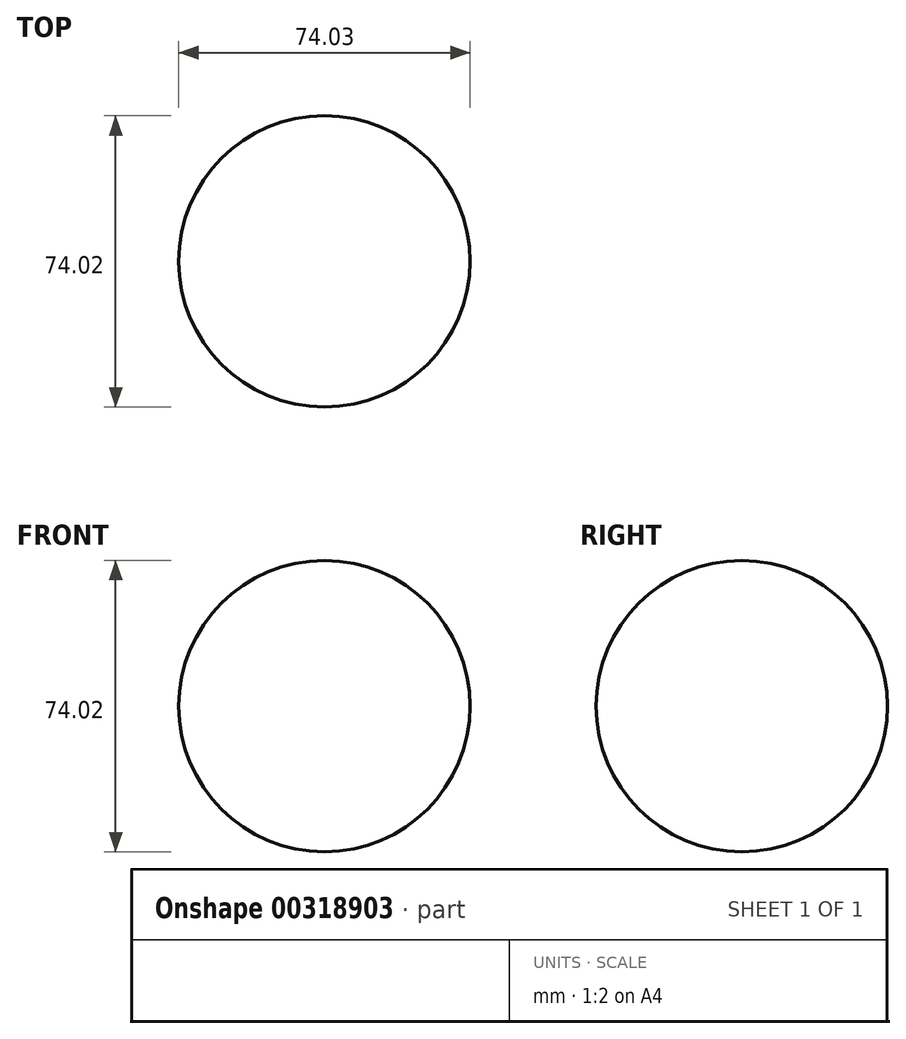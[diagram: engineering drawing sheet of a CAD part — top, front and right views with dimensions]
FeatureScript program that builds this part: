
annotation { "Feature Type Name" : "Feature", "Feature Type Description" : "" }
export const myFeature = defineFeature(function(context is Context, id is Id, definition is map)
    precondition{}
    {
        {
            var Q0;
            Q0=qCreatedBy(makeId("Front.planeOp"),FACE);
            var sketch = newSketch(context, id + "F0", { "sketchPlane" : qUnion([Q0])});
            skArc(sketch, "E0", {"start": v(39.62, 0) * mm, "mid": v(2.6, 37.01) * mm, "end": v(-34.41, 0) * mm});
            skLineSegment(sketch, "E1", {"start": v(-34.41, 0) * mm, "end": v(39.62, 0) * mm});
            skSolve(sketch);
        }
        {
            var Q0;
            Q0 = qSketchRegion(id + "F0", true);
            var Q1;
            Q1=sQuery(id+"F0.wireOp",EDGE,"E1");
            revolve(context, id + "F1", {"entities" : qUnion([Q0]), "axis" : qUnion([Q1]), "revolveType" : RevolveType.FULL});
        }
    });
